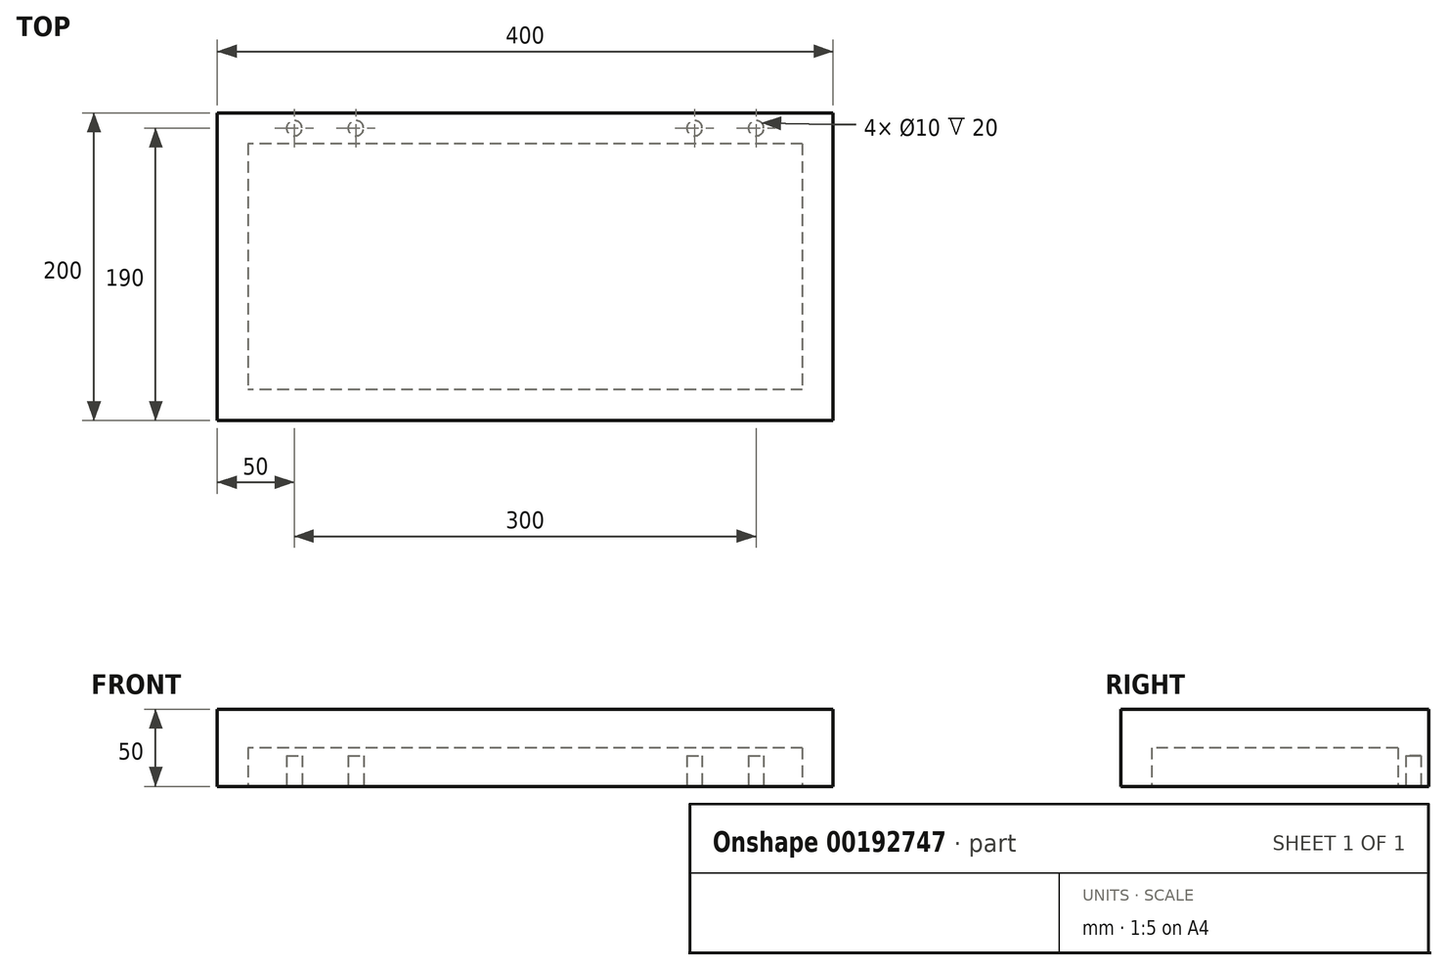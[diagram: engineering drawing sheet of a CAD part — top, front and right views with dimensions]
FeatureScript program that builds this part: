
annotation { "Feature Type Name" : "Feature", "Feature Type Description" : "" }
export const myFeature = defineFeature(function(context is Context, id is Id, definition is map)
    precondition{}
    {
        {
            var Q0;
            Q0=qCreatedBy(makeId("Top.planeOp"),FACE);
            var sketch = newSketch(context, id + "F0", { "sketchPlane" : qUnion([Q0])});
            skLineSegment(sketch, "E0.bottom", {"start": v(200, -100) * mm, "end": v(-200, -100) * mm});
            skLineSegment(sketch, "E0.top", {"start": v(200, 100) * mm, "end": v(-200, 100) * mm});
            skLineSegment(sketch, "E0.left", {"start": v(200, -100) * mm, "end": v(200, 100) * mm});
            skLineSegment(sketch, "E0.right", {"start": v(-200, -100) * mm, "end": v(-200, 100) * mm});
            skPoint(sketch, "E0.middle", {"position": v(0, 0) * mm});
            skSolve(sketch);
        }
        {
            var Q0;
            Q0 = qSketchRegion(id + "F0", true);
            extrude(context, id + "F1", {"entities" : qUnion([Q0]), "depth" : 50 * mm});
        }
        {
            var Q0;
            Q0=makeQuery(id+"F1.opExtrude","CAP_FACE",FACE,{"disambiguationData":[OSD([sQuery(id+"F0.wireOp",EDGE,"E0.bottom"),sQuery(id+"F0.wireOp",EDGE,"E0.top"),sQuery(id+"F0.wireOp",EDGE,"E0.left"),sQuery(id+"F0.wireOp",EDGE,"E0.right")])],"isStart":true});
            var sketch = newSketch(context, id + "F2", { "sketchPlane" : qUnion([Q0])});
            skLineSegment(sketch, "E1.bottom", {"start": v(180, -80) * mm, "end": v(-180, -80) * mm});
            skLineSegment(sketch, "E1.top", {"start": v(180, 80) * mm, "end": v(-180, 80) * mm});
            skLineSegment(sketch, "E1.left", {"start": v(180, -80) * mm, "end": v(180, 80) * mm});
            skLineSegment(sketch, "E1.right", {"start": v(-180, -80) * mm, "end": v(-180, 80) * mm});
            skPoint(sketch, "E1.middle", {"position": v(0, 0) * mm});
            skSolve(sketch);
        }
        {
            var Q0;
            Q0 = qSketchRegion(id + "F2", true);
            extrude(context, id + "F3", {"entities" : qUnion([Q0]), "operationType" : NewBodyOperationType.REMOVE, "oppositeDirection" : true, "depth" : 25 * mm});
        }
        {
            var Q0;
            Q0=makeQuery(id+"F1.opExtrude","CAP_FACE",FACE,{"disambiguationData":[OSD([sQuery(id+"F0.wireOp",EDGE,"E0.bottom"),sQuery(id+"F0.wireOp",EDGE,"E0.top"),sQuery(id+"F0.wireOp",EDGE,"E0.left"),sQuery(id+"F0.wireOp",EDGE,"E0.right")])],"isStart":true});
            var sketch = newSketch(context, id + "F4", { "sketchPlane" : qUnion([Q0])});
            skCircle(sketch, "E2", {"center": v(-150, -90) * mm, "radius": 5 * mm});
            skCircle(sketch, "E3", {"center": v(-110, -90) * mm, "radius": 5 * mm});
            skLineSegment(sketch, "E4", {"start": v(0, -80) * mm, "end": v(0, -100) * mm, "construction": true});
            skCircle(sketch, "E5.MirrorC", {"center": v(110, -90) * mm, "radius": 5 * mm});
            skCircle(sketch, "E6.MirrorC", {"center": v(150, -90) * mm, "radius": 5 * mm});
            skSolve(sketch);
        }
        {
            var Q0;
            Q0 = qSketchRegion(id + "F4", true);
            extrude(context, id + "F5", {"entities" : qUnion([Q0]), "operationType" : NewBodyOperationType.REMOVE, "oppositeDirection" : true, "depth" : 20 * mm});
        }
    });
